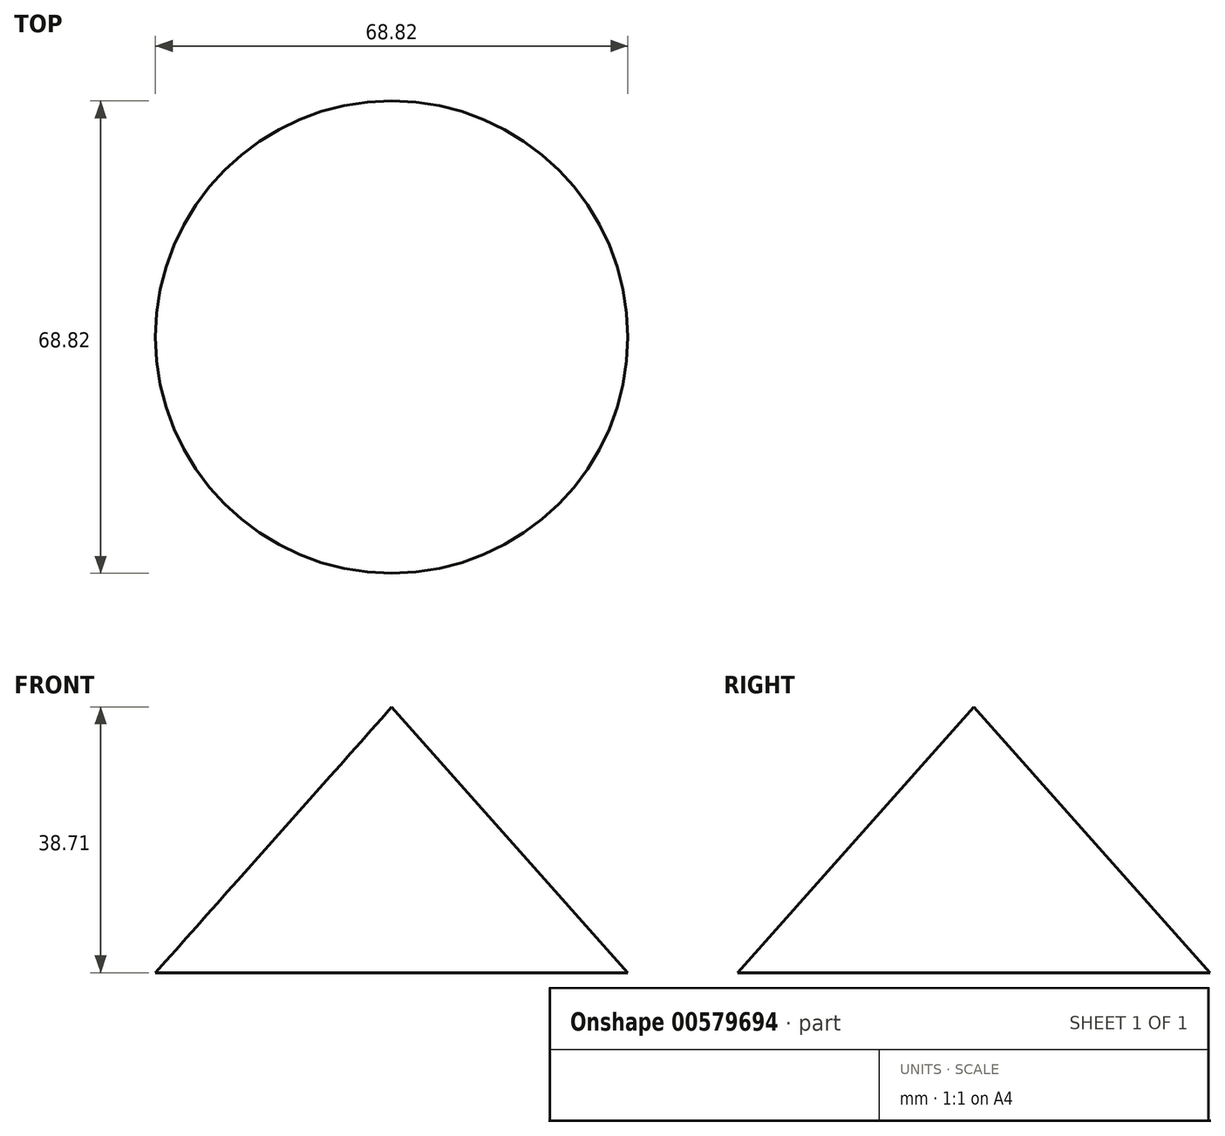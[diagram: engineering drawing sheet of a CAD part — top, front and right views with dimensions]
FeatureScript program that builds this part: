
annotation { "Feature Type Name" : "Feature", "Feature Type Description" : "" }
export const myFeature = defineFeature(function(context is Context, id is Id, definition is map)
    precondition{}
    {
        {
            var Q0;
            Q0=qCreatedBy(makeId("Front.planeOp"),FACE);
            var sketch = newSketch(context, id + "F0", { "sketchPlane" : qUnion([Q0])});
            skLineSegment(sketch, "E0", {"start": v(0, 0) * mm, "end": v(0, 38.7) * mm});
            skLineSegment(sketch, "E1", {"start": v(0, 38.7) * mm, "end": v(34.41, 0) * mm});
            skLineSegment(sketch, "E2", {"start": v(34.41, 0) * mm, "end": v(0, 0) * mm});
            skSolve(sketch);
        }
        {
            var Q0;
            Q0=makeQuery(id+"F0.imprint","IMPRINT",FACE,{"disambiguationData":[TD([[makeQuery(id+"F0.imprint","IMPRINT",EDGE,{"derivedFrom":sQuery(id+"F0.wireOp",EDGE,"E0")}),-1.0]])]});
            var Q1;
            Q1=sQuery(id+"F0.wireOp",EDGE,"E0");
            revolve(context, id + "F1", {"entities" : qUnion([Q0]), "axis" : qUnion([Q1]), "revolveType" : RevolveType.FULL});
        }
    });
